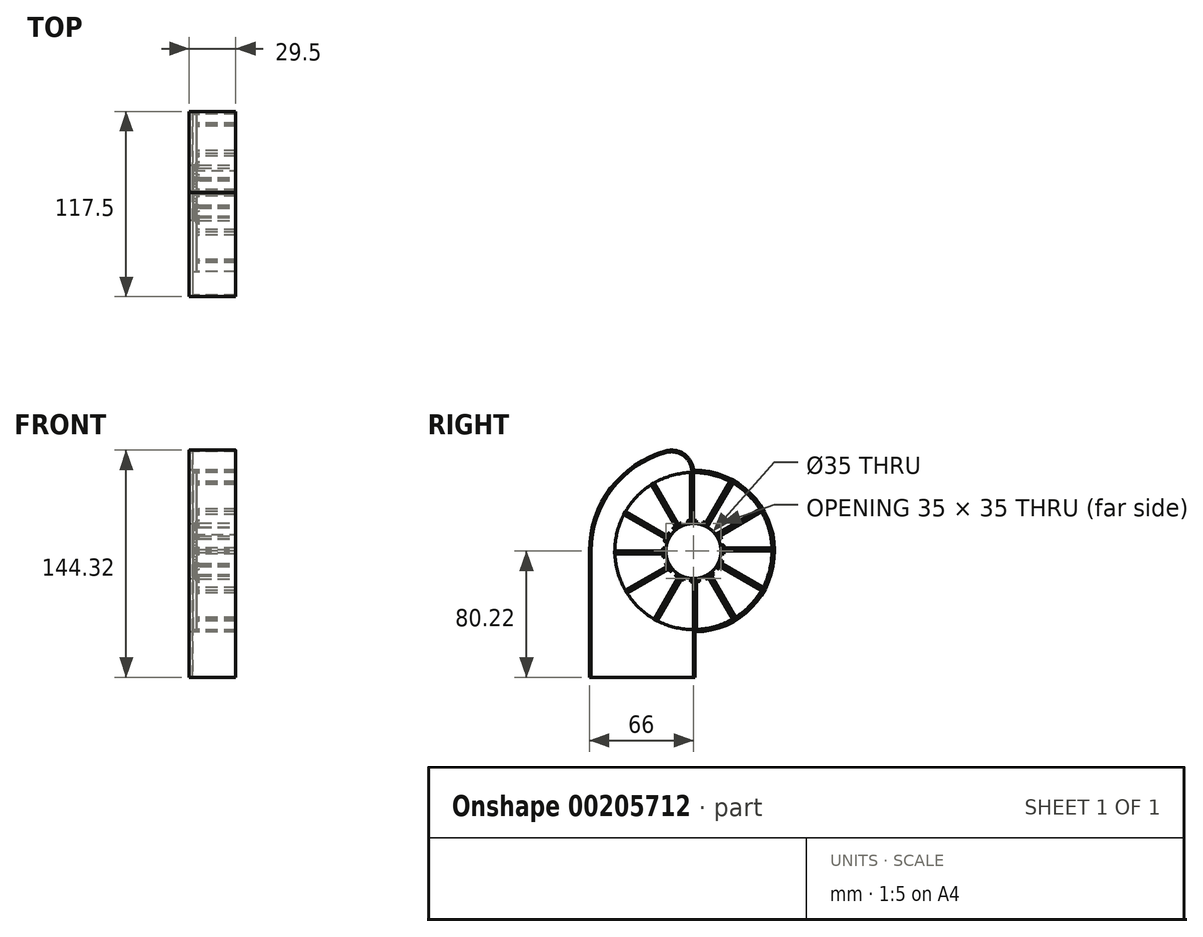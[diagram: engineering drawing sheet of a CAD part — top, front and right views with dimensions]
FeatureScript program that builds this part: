
annotation { "Feature Type Name" : "Feature", "Feature Type Description" : "" }
export const myFeature = defineFeature(function(context is Context, id is Id, definition is map)
    precondition{}
    {
        {
            var Q0;
            Q0=qCreatedBy(makeId("Front.planeOp"),FACE);
            var sketch = newSketch(context, id + "F0", { "sketchPlane" : qUnion([Q0])});
            skLineSegment(sketch, "E0", {"start": v(0, 0) * mm, "end": v(-1, 0) * mm});
            skLineSegment(sketch, "E1", {"start": v(-1, 0) * mm, "end": v(-1, 50) * mm});
            skLineSegment(sketch, "E2", {"start": v(-1, 50) * mm, "end": v(1, 50) * mm});
            skLineSegment(sketch, "E3", {"start": v(1, 50) * mm, "end": v(1, 0) * mm});
            skLineSegment(sketch, "E4", {"start": v(1, 0) * mm, "end": v(0, 0) * mm});
            skSolve(sketch);
        }
        {
            var Q0;
            Q0 = qSketchRegion(id + "F0", true);
            extrude(context, id + "F1", {"entities" : qUnion([Q0]), "depth" : 25 * mm, "offsetDistance" : 25 * mm});
        }
        {
            var Q0;
            Q0=makeQuery(id+"F1.opExtrude","SWEPT_BODY",BODY,{"disambiguationData":[OSD([sQuery(id+"F0.wireOp",EDGE,"E0"),sQuery(id+"F0.wireOp",EDGE,"E1"),sQuery(id+"F0.wireOp",EDGE,"E2"),sQuery(id+"F0.wireOp",EDGE,"E3"),sQuery(id+"F0.wireOp",EDGE,"E4")])]});
            var Q1;
            Q1=sQuery(id+"F0.wireOp",EDGE,"E1");
            var Q2;
            Q2=sQuery(id+"F0.wireOp",EDGE,"E1");
            transform(context, id + "F2", {"entities" : qUnion([Q0]), "transformType" : TransformType.ROTATION, "transformAxis" : qUnion([Q2]), "angle" : 90 * degree, "makeCopy" : false});
        }
        {
            var Q0;
            Q0=makeQuery(id+"F1.opExtrude","SWEPT_BODY",BODY,{"disambiguationData":[OSD([sQuery(id+"F0.wireOp",EDGE,"E0"),sQuery(id+"F0.wireOp",EDGE,"E1"),sQuery(id+"F0.wireOp",EDGE,"E2"),sQuery(id+"F0.wireOp",EDGE,"E3"),sQuery(id+"F0.wireOp",EDGE,"E4")])]});
            var Q1;
            Q1=makeQuery(id+"F1.opExtrude","SWEPT_EDGE",EDGE,{"disambiguationData":[OSD([sQuery(id+"F0.wireOp",EDGE,"E3"),sQuery(id+"F0.wireOp",EDGE,"E4")])]});
            circularPattern(context, id + "F3", {"entities" : qUnion([Q0]), "axis" : qUnion([Q1]), "angle" : 360 * degree, "instanceCount" : 12, "oppositeDirection" : true, "equalSpace" : true});
        }
        {
            var Q0;
            Q0=makeQuery(id+"F3.opPattern","COPY",FACE,{"derivedFrom":makeQuery(id+"F1.opExtrude","CAP_FACE",FACE,{"disambiguationData":[OSD([sQuery(id+"F0.wireOp",EDGE,"E0"),sQuery(id+"F0.wireOp",EDGE,"E1"),sQuery(id+"F0.wireOp",EDGE,"E2"),sQuery(id+"F0.wireOp",EDGE,"E3"),sQuery(id+"F0.wireOp",EDGE,"E4")])],"isStart":true}),"instanceName":"10"});
            var sketch = newSketch(context, id + "F4", { "sketchPlane" : qUnion([Q0])});
            skCircle(sketch, "E5", {"center": v(-2, 0) * mm, "radius": 49.91 * mm});
            skSolve(sketch);
        }
        {
            var Q0;
            Q0 = qSketchRegion(id + "F4", true);
            extrude(context, id + "F5", {"entities" : qUnion([Q0]), "operationType" : NewBodyOperationType.ADD, "depth" : 2 * mm, "offsetDistance" : 25 * mm});
        }
        {
            var Q0;
            Q0=makeQuery(id+"F3.opPattern","COPY",FACE,{"derivedFrom":makeQuery(id+"F1.opExtrude","CAP_FACE",FACE,{"disambiguationData":[OSD([sQuery(id+"F0.wireOp",EDGE,"E0"),sQuery(id+"F0.wireOp",EDGE,"E1"),sQuery(id+"F0.wireOp",EDGE,"E2"),sQuery(id+"F0.wireOp",EDGE,"E3"),sQuery(id+"F0.wireOp",EDGE,"E4")])],"isStart":false}),"instanceName":"9"});
            var sketch = newSketch(context, id + "F6", { "sketchPlane" : qUnion([Q0])});
            skCircle(sketch, "E6", {"center": v(2, 0) * mm, "radius": 17.5 * mm});
            skSolve(sketch);
        }
        {
            var Q0;
            Q0 = qSketchRegion(id + "F6", true);
            extrude(context, id + "F7", {"entities" : qUnion([Q0]), "operationType" : NewBodyOperationType.REMOVE, "oppositeDirection" : true, "depth" : 30 * mm, "offsetDistance" : 25 * mm});
        }
        {
            var Q0;
            {var subQ0=sQuery(id+"F0.wireOp",EDGE,"E1");Q0=makeQuery(id+"F5.boolean.opBoolean","SPLIT",EDGE,{"disambiguationData":[topologyDisambiguationEdgeConnected([makeQuery(id+"F5.opExtrude","CAP_FACE",FACE,{"disambiguationData":[OSD([sQuery(id+"F4.wireOp",EDGE,"E5")])],"isStart":true})])],"derivedFrom":makeQuery(id+"F3.opPattern","COPY",EDGE,{"derivedFrom":makeQuery(id+"F1.opExtrude","CAP_EDGE",EDGE,{"disambiguationData":[OSD([subQ0])],"isStart":true}),"instanceName":"5"})});}
            var Q1;
            {var subQ0=sQuery(id+"F0.wireOp",EDGE,"E3");Q1=makeQuery(id+"F5.boolean.opBoolean","SPLIT",EDGE,{"disambiguationData":[topologyDisambiguationEdgeConnected([makeQuery(id+"F5.opExtrude","CAP_FACE",FACE,{"disambiguationData":[OSD([sQuery(id+"F4.wireOp",EDGE,"E5")])],"isStart":true})])],"derivedFrom":makeQuery(id+"F3.opPattern","COPY",EDGE,{"derivedFrom":makeQuery(id+"F1.opExtrude","CAP_EDGE",EDGE,{"disambiguationData":[OSD([subQ0])],"isStart":true}),"instanceName":"6"})});}
            var Q2;
            {var subQ0=sQuery(id+"F0.wireOp",EDGE,"E1");Q2=makeQuery(id+"F5.boolean.opBoolean","SPLIT",EDGE,{"disambiguationData":[topologyDisambiguationEdgeConnected([makeQuery(id+"F5.opExtrude","CAP_FACE",FACE,{"disambiguationData":[OSD([sQuery(id+"F4.wireOp",EDGE,"E5")])],"isStart":true})])],"derivedFrom":makeQuery(id+"F3.opPattern","COPY",EDGE,{"derivedFrom":makeQuery(id+"F1.opExtrude","CAP_EDGE",EDGE,{"disambiguationData":[OSD([subQ0])],"isStart":true}),"instanceName":"10"})});}
            var Q3;
            {var subQ0=sQuery(id+"F0.wireOp",EDGE,"E3");Q3=makeQuery(id+"F5.boolean.opBoolean","SPLIT",EDGE,{"disambiguationData":[topologyDisambiguationEdgeConnected([makeQuery(id+"F5.opExtrude","CAP_FACE",FACE,{"disambiguationData":[OSD([sQuery(id+"F4.wireOp",EDGE,"E5")])],"isStart":true})])],"derivedFrom":makeQuery(id+"F3.opPattern","COPY",EDGE,{"derivedFrom":makeQuery(id+"F1.opExtrude","CAP_EDGE",EDGE,{"disambiguationData":[OSD([subQ0])],"isStart":true}),"instanceName":"11"})});}
            var Q4;
            {var subQ0=sQuery(id+"F0.wireOp",EDGE,"E3");Q4=makeQuery(id+"F5.boolean.opBoolean","SPLIT",EDGE,{"disambiguationData":[topologyDisambiguationEdgeConnected([makeQuery(id+"F5.opExtrude","CAP_FACE",FACE,{"disambiguationData":[OSD([sQuery(id+"F4.wireOp",EDGE,"E5")])],"isStart":true})])],"derivedFrom":makeQuery(id+"F1.opExtrude","CAP_EDGE",EDGE,{"disambiguationData":[OSD([subQ0])],"isStart":true})});}
            var Q5;
            {var subQ0=sQuery(id+"F0.wireOp",EDGE,"E1");Q5=makeQuery(id+"F5.boolean.opBoolean","SPLIT",EDGE,{"disambiguationData":[topologyDisambiguationEdgeConnected([makeQuery(id+"F5.opExtrude","CAP_FACE",FACE,{"disambiguationData":[OSD([sQuery(id+"F4.wireOp",EDGE,"E5")])],"isStart":true})])],"derivedFrom":makeQuery(id+"F3.opPattern","COPY",EDGE,{"derivedFrom":makeQuery(id+"F1.opExtrude","CAP_EDGE",EDGE,{"disambiguationData":[OSD([subQ0])],"isStart":true}),"instanceName":"11"})});}
            var Q6;
            {var subQ0=sQuery(id+"F0.wireOp",EDGE,"E1");Q6=makeQuery(id+"F5.boolean.opBoolean","SPLIT",EDGE,{"disambiguationData":[topologyDisambiguationEdgeConnected([makeQuery(id+"F5.opExtrude","CAP_FACE",FACE,{"disambiguationData":[OSD([sQuery(id+"F4.wireOp",EDGE,"E5")])],"isStart":true})])],"derivedFrom":makeQuery(id+"F1.opExtrude","CAP_EDGE",EDGE,{"disambiguationData":[OSD([subQ0])],"isStart":true})});}
            var Q7;
            {var subQ0=sQuery(id+"F0.wireOp",EDGE,"E3");Q7=makeQuery(id+"F5.boolean.opBoolean","SPLIT",EDGE,{"disambiguationData":[topologyDisambiguationEdgeConnected([makeQuery(id+"F5.opExtrude","CAP_FACE",FACE,{"disambiguationData":[OSD([sQuery(id+"F4.wireOp",EDGE,"E5")])],"isStart":true})])],"derivedFrom":makeQuery(id+"F3.opPattern","COPY",EDGE,{"derivedFrom":makeQuery(id+"F1.opExtrude","CAP_EDGE",EDGE,{"disambiguationData":[OSD([subQ0])],"isStart":true}),"instanceName":"1"})});}
            var Q8;
            {var subQ0=sQuery(id+"F0.wireOp",EDGE,"E1");Q8=makeQuery(id+"F5.boolean.opBoolean","SPLIT",EDGE,{"disambiguationData":[topologyDisambiguationEdgeConnected([makeQuery(id+"F5.opExtrude","CAP_FACE",FACE,{"disambiguationData":[OSD([sQuery(id+"F4.wireOp",EDGE,"E5")])],"isStart":true})])],"derivedFrom":makeQuery(id+"F3.opPattern","COPY",EDGE,{"derivedFrom":makeQuery(id+"F1.opExtrude","CAP_EDGE",EDGE,{"disambiguationData":[OSD([subQ0])],"isStart":true}),"instanceName":"1"})});}
            var Q9;
            {var subQ0=sQuery(id+"F0.wireOp",EDGE,"E1");Q9=makeQuery(id+"F5.boolean.opBoolean","SPLIT",EDGE,{"disambiguationData":[topologyDisambiguationEdgeConnected([makeQuery(id+"F5.opExtrude","CAP_FACE",FACE,{"disambiguationData":[OSD([sQuery(id+"F4.wireOp",EDGE,"E5")])],"isStart":true})])],"derivedFrom":makeQuery(id+"F3.opPattern","COPY",EDGE,{"derivedFrom":makeQuery(id+"F1.opExtrude","CAP_EDGE",EDGE,{"disambiguationData":[OSD([subQ0])],"isStart":true}),"instanceName":"2"})});}
            var Q10;
            {var subQ0=sQuery(id+"F0.wireOp",EDGE,"E1");Q10=makeQuery(id+"F5.boolean.opBoolean","SPLIT",EDGE,{"disambiguationData":[topologyDisambiguationEdgeConnected([makeQuery(id+"F5.opExtrude","CAP_FACE",FACE,{"disambiguationData":[OSD([sQuery(id+"F4.wireOp",EDGE,"E5")])],"isStart":true})])],"derivedFrom":makeQuery(id+"F3.opPattern","COPY",EDGE,{"derivedFrom":makeQuery(id+"F1.opExtrude","CAP_EDGE",EDGE,{"disambiguationData":[OSD([subQ0])],"isStart":true}),"instanceName":"3"})});}
            var Q11;
            {var subQ0=sQuery(id+"F0.wireOp",EDGE,"E1");Q11=makeQuery(id+"F5.boolean.opBoolean","SPLIT",EDGE,{"disambiguationData":[topologyDisambiguationEdgeConnected([makeQuery(id+"F5.opExtrude","CAP_FACE",FACE,{"disambiguationData":[OSD([sQuery(id+"F4.wireOp",EDGE,"E5")])],"isStart":true})])],"derivedFrom":makeQuery(id+"F3.opPattern","COPY",EDGE,{"derivedFrom":makeQuery(id+"F1.opExtrude","CAP_EDGE",EDGE,{"disambiguationData":[OSD([subQ0])],"isStart":true}),"instanceName":"4"})});}
            var Q12;
            {var subQ0=sQuery(id+"F0.wireOp",EDGE,"E1");Q12=makeQuery(id+"F5.boolean.opBoolean","SPLIT",EDGE,{"disambiguationData":[topologyDisambiguationEdgeConnected([makeQuery(id+"F5.opExtrude","CAP_FACE",FACE,{"disambiguationData":[OSD([sQuery(id+"F4.wireOp",EDGE,"E5")])],"isStart":true})])],"derivedFrom":makeQuery(id+"F3.opPattern","COPY",EDGE,{"derivedFrom":makeQuery(id+"F1.opExtrude","CAP_EDGE",EDGE,{"disambiguationData":[OSD([subQ0])],"isStart":true}),"instanceName":"6"})});}
            var Q13;
            {var subQ0=sQuery(id+"F0.wireOp",EDGE,"E3");Q13=makeQuery(id+"F5.boolean.opBoolean","SPLIT",EDGE,{"disambiguationData":[topologyDisambiguationEdgeConnected([makeQuery(id+"F5.opExtrude","CAP_FACE",FACE,{"disambiguationData":[OSD([sQuery(id+"F4.wireOp",EDGE,"E5")])],"isStart":true})])],"derivedFrom":makeQuery(id+"F3.opPattern","COPY",EDGE,{"derivedFrom":makeQuery(id+"F1.opExtrude","CAP_EDGE",EDGE,{"disambiguationData":[OSD([subQ0])],"isStart":true}),"instanceName":"7"})});}
            var Q14;
            Q14=makeQuery(id+"F5.boolean.opBoolean","MERGE",EDGE,{"derivedFrom":[makeQuery(id+"F3.opPattern","COPY",EDGE,{"derivedFrom":makeQuery(id+"F1.opExtrude","CAP_EDGE",EDGE,{"disambiguationData":[OSD([sQuery(id+"F0.wireOp",EDGE,"E3")])],"isStart":true}),"instanceName":"8"}),makeQuery(id+"F3.opPattern","COPY",EDGE,{"derivedFrom":makeQuery(id+"F1.opExtrude","CAP_EDGE",EDGE,{"disambiguationData":[OSD([sQuery(id+"F0.wireOp",EDGE,"E0"),sQuery(id+"F0.wireOp",EDGE,"E4")])],"isStart":true}),"instanceName":"11"})]});
            var Q15;
            {var subQ0=sQuery(id+"F0.wireOp",EDGE,"E3");Q15=makeQuery(id+"F5.boolean.opBoolean","SPLIT",EDGE,{"disambiguationData":[topologyDisambiguationEdgeConnected([makeQuery(id+"F5.opExtrude","CAP_FACE",FACE,{"disambiguationData":[OSD([sQuery(id+"F4.wireOp",EDGE,"E5")])],"isStart":true})])],"derivedFrom":makeQuery(id+"F3.opPattern","COPY",EDGE,{"derivedFrom":makeQuery(id+"F1.opExtrude","CAP_EDGE",EDGE,{"disambiguationData":[OSD([subQ0])],"isStart":true}),"instanceName":"9"})});}
            var Q16;
            {var subQ0=sQuery(id+"F0.wireOp",EDGE,"E3");Q16=makeQuery(id+"F5.boolean.opBoolean","SPLIT",EDGE,{"disambiguationData":[topologyDisambiguationEdgeConnected([makeQuery(id+"F5.opExtrude","CAP_FACE",FACE,{"disambiguationData":[OSD([sQuery(id+"F4.wireOp",EDGE,"E5")])],"isStart":true})])],"derivedFrom":makeQuery(id+"F3.opPattern","COPY",EDGE,{"derivedFrom":makeQuery(id+"F1.opExtrude","CAP_EDGE",EDGE,{"disambiguationData":[OSD([subQ0])],"isStart":true}),"instanceName":"10"})});}
            var Q17;
            {var subQ0=sQuery(id+"F0.wireOp",EDGE,"E3");Q17=makeQuery(id+"F5.boolean.opBoolean","SPLIT",EDGE,{"disambiguationData":[topologyDisambiguationEdgeConnected([makeQuery(id+"F5.opExtrude","CAP_FACE",FACE,{"disambiguationData":[OSD([sQuery(id+"F4.wireOp",EDGE,"E5")])],"isStart":true})])],"derivedFrom":makeQuery(id+"F3.opPattern","COPY",EDGE,{"derivedFrom":makeQuery(id+"F1.opExtrude","CAP_EDGE",EDGE,{"disambiguationData":[OSD([subQ0])],"isStart":true}),"instanceName":"2"})});}
            var Q18;
            {var subQ0=sQuery(id+"F0.wireOp",EDGE,"E3");Q18=makeQuery(id+"F5.boolean.opBoolean","SPLIT",EDGE,{"disambiguationData":[topologyDisambiguationEdgeConnected([makeQuery(id+"F5.opExtrude","CAP_FACE",FACE,{"disambiguationData":[OSD([sQuery(id+"F4.wireOp",EDGE,"E5")])],"isStart":true})])],"derivedFrom":makeQuery(id+"F3.opPattern","COPY",EDGE,{"derivedFrom":makeQuery(id+"F1.opExtrude","CAP_EDGE",EDGE,{"disambiguationData":[OSD([subQ0])],"isStart":true}),"instanceName":"3"})});}
            var Q19;
            {var subQ0=sQuery(id+"F0.wireOp",EDGE,"E1");Q19=makeQuery(id+"F5.boolean.opBoolean","SPLIT",EDGE,{"disambiguationData":[topologyDisambiguationEdgeConnected([makeQuery(id+"F5.opExtrude","CAP_FACE",FACE,{"disambiguationData":[OSD([sQuery(id+"F4.wireOp",EDGE,"E5")])],"isStart":true})])],"derivedFrom":makeQuery(id+"F3.opPattern","COPY",EDGE,{"derivedFrom":makeQuery(id+"F1.opExtrude","CAP_EDGE",EDGE,{"disambiguationData":[OSD([subQ0])],"isStart":true}),"instanceName":"8"})});}
            var Q20;
            {var subQ0=sQuery(id+"F0.wireOp",EDGE,"E1");Q20=makeQuery(id+"F5.boolean.opBoolean","SPLIT",EDGE,{"disambiguationData":[topologyDisambiguationEdgeConnected([makeQuery(id+"F5.opExtrude","CAP_FACE",FACE,{"disambiguationData":[OSD([sQuery(id+"F4.wireOp",EDGE,"E5")])],"isStart":true})])],"derivedFrom":makeQuery(id+"F3.opPattern","COPY",EDGE,{"derivedFrom":makeQuery(id+"F1.opExtrude","CAP_EDGE",EDGE,{"disambiguationData":[OSD([subQ0])],"isStart":true}),"instanceName":"9"})});}
            var Q21;
            {var subQ0=sQuery(id+"F0.wireOp",EDGE,"E1");Q21=makeQuery(id+"F5.boolean.opBoolean","SPLIT",EDGE,{"disambiguationData":[topologyDisambiguationEdgeConnected([makeQuery(id+"F5.opExtrude","CAP_FACE",FACE,{"disambiguationData":[OSD([sQuery(id+"F4.wireOp",EDGE,"E5")])],"isStart":true})])],"derivedFrom":makeQuery(id+"F3.opPattern","COPY",EDGE,{"derivedFrom":makeQuery(id+"F1.opExtrude","CAP_EDGE",EDGE,{"disambiguationData":[OSD([subQ0])],"isStart":true}),"instanceName":"7"})});}
            var Q22;
            {var subQ0=sQuery(id+"F0.wireOp",EDGE,"E3");Q22=makeQuery(id+"F5.boolean.opBoolean","SPLIT",EDGE,{"disambiguationData":[topologyDisambiguationEdgeConnected([makeQuery(id+"F5.opExtrude","CAP_FACE",FACE,{"disambiguationData":[OSD([sQuery(id+"F4.wireOp",EDGE,"E5")])],"isStart":true})])],"derivedFrom":makeQuery(id+"F3.opPattern","COPY",EDGE,{"derivedFrom":makeQuery(id+"F1.opExtrude","CAP_EDGE",EDGE,{"disambiguationData":[OSD([subQ0])],"isStart":true}),"instanceName":"5"})});}
            var Q23;
            {var subQ0=sQuery(id+"F0.wireOp",EDGE,"E3");Q23=makeQuery(id+"F5.boolean.opBoolean","SPLIT",EDGE,{"disambiguationData":[topologyDisambiguationEdgeConnected([makeQuery(id+"F5.opExtrude","CAP_FACE",FACE,{"disambiguationData":[OSD([sQuery(id+"F4.wireOp",EDGE,"E5")])],"isStart":true})])],"derivedFrom":makeQuery(id+"F3.opPattern","COPY",EDGE,{"derivedFrom":makeQuery(id+"F1.opExtrude","CAP_EDGE",EDGE,{"disambiguationData":[OSD([subQ0])],"isStart":true}),"instanceName":"4"})});}
            fillet(context, id + "F8", {"entities" : qUnion([Q0, Q1, Q2, Q3, Q4, Q5, Q6, Q7, Q8, Q9, Q10, Q11, Q12, Q13, Q14, Q15, Q16, Q17, Q18, Q19, Q20, Q21, Q22, Q23]), "radius" : 2 * mm, "tangentPropagation" : true, "allowEdgeOverflow" : false});
        }
        {
            var Q0;
            {var subQ0=sQuery(id+"F0.wireOp",EDGE,"E1");Q0=makeQuery(id+"F8.opFillet","BLEND_EDGE",EDGE,{"blendedFrom":[makeQuery(id+"F5.boolean.opBoolean","SPLIT",EDGE,{"disambiguationData":[topologyDisambiguationEdgeConnected([makeQuery(id+"F5.opExtrude","CAP_FACE",FACE,{"disambiguationData":[OSD([sQuery(id+"F4.wireOp",EDGE,"E5")])],"isStart":true})])],"derivedFrom":makeQuery(id+"F3.opPattern","COPY",EDGE,{"derivedFrom":makeQuery(id+"F1.opExtrude","CAP_EDGE",EDGE,{"disambiguationData":[OSD([subQ0])],"isStart":true}),"instanceName":"4"})}),makeQuery(id+"F7.boolean.opBoolean","COPY",FACE,{"derivedFrom":makeQuery(id+"F7.opExtrude","SWEPT_FACE",FACE,{"disambiguationData":[OSD([sQuery(id+"F6.wireOp",EDGE,"E6")])]})})],"blendedInto":[makeQuery(id+"F7.boolean.opBoolean","COPY",FACE,{"derivedFrom":makeQuery(id+"F7.opExtrude","SWEPT_FACE",FACE,{"disambiguationData":[OSD([sQuery(id+"F6.wireOp",EDGE,"E6")])]})})]});}
            var Q1;
            {var subQ1=sQuery(id+"F0.wireOp",EDGE,"E1");var subQ3=sQuery(id+"F4.wireOp",EDGE,"E5");Q1=makeQuery(id+"F7.boolean.opBoolean","INTERSECT",EDGE,{"derivedFrom":[makeQuery(id+"F5.boolean.opBoolean","SPLIT",FACE,{"disambiguationData":[TD([makeQuery(id+"F3.opPattern","COPY",FACE,{"derivedFrom":makeQuery(id+"F1.opExtrude","SWEPT_FACE",FACE,{"disambiguationData":[OSD([subQ1])]}),"instanceName":"3"})])],"derivedFrom":makeQuery(id+"F5.opExtrude","CAP_FACE",FACE,{"disambiguationData":[OSD([subQ3])],"isStart":true})}),makeQuery(id+"F7.opExtrude","SWEPT_FACE",FACE,{"disambiguationData":[OSD([sQuery(id+"F6.wireOp",EDGE,"E6")])]})]});}
            var Q2;
            {var subQ1=sQuery(id+"F0.wireOp",EDGE,"E1");var subQ3=sQuery(id+"F4.wireOp",EDGE,"E5");Q2=makeQuery(id+"F7.boolean.opBoolean","INTERSECT",EDGE,{"derivedFrom":[makeQuery(id+"F5.boolean.opBoolean","SPLIT",FACE,{"disambiguationData":[TD([makeQuery(id+"F3.opPattern","COPY",FACE,{"derivedFrom":makeQuery(id+"F1.opExtrude","SWEPT_FACE",FACE,{"disambiguationData":[OSD([subQ1])]}),"instanceName":"2"})])],"derivedFrom":makeQuery(id+"F5.opExtrude","CAP_FACE",FACE,{"disambiguationData":[OSD([subQ3])],"isStart":true})}),makeQuery(id+"F7.opExtrude","SWEPT_FACE",FACE,{"disambiguationData":[OSD([sQuery(id+"F6.wireOp",EDGE,"E6")])]})]});}
            var Q3;
            {var subQ0=sQuery(id+"F0.wireOp",EDGE,"E1");Q3=makeQuery(id+"F8.opFillet","BLEND_EDGE",EDGE,{"blendedFrom":[makeQuery(id+"F5.boolean.opBoolean","SPLIT",EDGE,{"disambiguationData":[topologyDisambiguationEdgeConnected([makeQuery(id+"F5.opExtrude","CAP_FACE",FACE,{"disambiguationData":[OSD([sQuery(id+"F4.wireOp",EDGE,"E5")])],"isStart":true})])],"derivedFrom":makeQuery(id+"F3.opPattern","COPY",EDGE,{"derivedFrom":makeQuery(id+"F1.opExtrude","CAP_EDGE",EDGE,{"disambiguationData":[OSD([subQ0])],"isStart":true}),"instanceName":"5"})}),makeQuery(id+"F7.boolean.opBoolean","COPY",FACE,{"derivedFrom":makeQuery(id+"F7.opExtrude","SWEPT_FACE",FACE,{"disambiguationData":[OSD([sQuery(id+"F6.wireOp",EDGE,"E6")])]})})],"blendedInto":[makeQuery(id+"F7.boolean.opBoolean","COPY",FACE,{"derivedFrom":makeQuery(id+"F7.opExtrude","SWEPT_FACE",FACE,{"disambiguationData":[OSD([sQuery(id+"F6.wireOp",EDGE,"E6")])]})})]});}
            var Q4;
            {var subQ0=sQuery(id+"F0.wireOp",EDGE,"E1");Q4=makeQuery(id+"F8.opFillet","BLEND_EDGE",EDGE,{"blendedFrom":[makeQuery(id+"F5.boolean.opBoolean","SPLIT",EDGE,{"disambiguationData":[topologyDisambiguationEdgeConnected([makeQuery(id+"F5.opExtrude","CAP_FACE",FACE,{"disambiguationData":[OSD([sQuery(id+"F4.wireOp",EDGE,"E5")])],"isStart":true})])],"derivedFrom":makeQuery(id+"F3.opPattern","COPY",EDGE,{"derivedFrom":makeQuery(id+"F1.opExtrude","CAP_EDGE",EDGE,{"disambiguationData":[OSD([subQ0])],"isStart":true}),"instanceName":"6"})}),makeQuery(id+"F7.boolean.opBoolean","COPY",FACE,{"derivedFrom":makeQuery(id+"F7.opExtrude","SWEPT_FACE",FACE,{"disambiguationData":[OSD([sQuery(id+"F6.wireOp",EDGE,"E6")])]})})],"blendedInto":[makeQuery(id+"F7.boolean.opBoolean","COPY",FACE,{"derivedFrom":makeQuery(id+"F7.opExtrude","SWEPT_FACE",FACE,{"disambiguationData":[OSD([sQuery(id+"F6.wireOp",EDGE,"E6")])]})})]});}
            var Q5;
            {var subQ0=sQuery(id+"F0.wireOp",EDGE,"E1");Q5=makeQuery(id+"F8.opFillet","BLEND_EDGE",EDGE,{"blendedFrom":[makeQuery(id+"F5.boolean.opBoolean","SPLIT",EDGE,{"disambiguationData":[topologyDisambiguationEdgeConnected([makeQuery(id+"F5.opExtrude","CAP_FACE",FACE,{"disambiguationData":[OSD([sQuery(id+"F4.wireOp",EDGE,"E5")])],"isStart":true})])],"derivedFrom":makeQuery(id+"F3.opPattern","COPY",EDGE,{"derivedFrom":makeQuery(id+"F1.opExtrude","CAP_EDGE",EDGE,{"disambiguationData":[OSD([subQ0])],"isStart":true}),"instanceName":"7"})}),makeQuery(id+"F7.boolean.opBoolean","COPY",FACE,{"derivedFrom":makeQuery(id+"F7.opExtrude","SWEPT_FACE",FACE,{"disambiguationData":[OSD([sQuery(id+"F6.wireOp",EDGE,"E6")])]})})],"blendedInto":[makeQuery(id+"F7.boolean.opBoolean","COPY",FACE,{"derivedFrom":makeQuery(id+"F7.opExtrude","SWEPT_FACE",FACE,{"disambiguationData":[OSD([sQuery(id+"F6.wireOp",EDGE,"E6")])]})})]});}
            var Q6;
            {var subQ0=sQuery(id+"F0.wireOp",EDGE,"E3");Q6=makeQuery(id+"F8.opFillet","BLEND_EDGE",EDGE,{"blendedFrom":[makeQuery(id+"F5.boolean.opBoolean","SPLIT",EDGE,{"disambiguationData":[topologyDisambiguationEdgeConnected([makeQuery(id+"F5.opExtrude","CAP_FACE",FACE,{"disambiguationData":[OSD([sQuery(id+"F4.wireOp",EDGE,"E5")])],"isStart":true})])],"derivedFrom":makeQuery(id+"F3.opPattern","COPY",EDGE,{"derivedFrom":makeQuery(id+"F1.opExtrude","CAP_EDGE",EDGE,{"disambiguationData":[OSD([subQ0])],"isStart":true}),"instanceName":"2"})}),makeQuery(id+"F7.boolean.opBoolean","COPY",FACE,{"derivedFrom":makeQuery(id+"F7.opExtrude","SWEPT_FACE",FACE,{"disambiguationData":[OSD([sQuery(id+"F6.wireOp",EDGE,"E6")])]})})],"blendedInto":[makeQuery(id+"F7.boolean.opBoolean","COPY",FACE,{"derivedFrom":makeQuery(id+"F7.opExtrude","SWEPT_FACE",FACE,{"disambiguationData":[OSD([sQuery(id+"F6.wireOp",EDGE,"E6")])]})})]});}
            var Q7;
            {var subQ0=sQuery(id+"F0.wireOp",EDGE,"E3");Q7=makeQuery(id+"F8.opFillet","BLEND_EDGE",EDGE,{"blendedFrom":[makeQuery(id+"F5.boolean.opBoolean","SPLIT",EDGE,{"disambiguationData":[topologyDisambiguationEdgeConnected([makeQuery(id+"F5.opExtrude","CAP_FACE",FACE,{"disambiguationData":[OSD([sQuery(id+"F4.wireOp",EDGE,"E5")])],"isStart":true})])],"derivedFrom":makeQuery(id+"F3.opPattern","COPY",EDGE,{"derivedFrom":makeQuery(id+"F1.opExtrude","CAP_EDGE",EDGE,{"disambiguationData":[OSD([subQ0])],"isStart":true}),"instanceName":"9"})}),makeQuery(id+"F7.boolean.opBoolean","COPY",FACE,{"derivedFrom":makeQuery(id+"F7.opExtrude","SWEPT_FACE",FACE,{"disambiguationData":[OSD([sQuery(id+"F6.wireOp",EDGE,"E6")])]})})],"blendedInto":[makeQuery(id+"F7.boolean.opBoolean","COPY",FACE,{"derivedFrom":makeQuery(id+"F7.opExtrude","SWEPT_FACE",FACE,{"disambiguationData":[OSD([sQuery(id+"F6.wireOp",EDGE,"E6")])]})})]});}
            var Q8;
            {var subQ0=sQuery(id+"F0.wireOp",EDGE,"E3");Q8=makeQuery(id+"F8.opFillet","BLEND_EDGE",EDGE,{"blendedFrom":[makeQuery(id+"F5.boolean.opBoolean","SPLIT",EDGE,{"disambiguationData":[topologyDisambiguationEdgeConnected([makeQuery(id+"F5.opExtrude","CAP_FACE",FACE,{"disambiguationData":[OSD([sQuery(id+"F4.wireOp",EDGE,"E5")])],"isStart":true})])],"derivedFrom":makeQuery(id+"F3.opPattern","COPY",EDGE,{"derivedFrom":makeQuery(id+"F1.opExtrude","CAP_EDGE",EDGE,{"disambiguationData":[OSD([subQ0])],"isStart":true}),"instanceName":"10"})}),makeQuery(id+"F7.boolean.opBoolean","COPY",FACE,{"derivedFrom":makeQuery(id+"F7.opExtrude","SWEPT_FACE",FACE,{"disambiguationData":[OSD([sQuery(id+"F6.wireOp",EDGE,"E6")])]})})],"blendedInto":[makeQuery(id+"F7.boolean.opBoolean","COPY",FACE,{"derivedFrom":makeQuery(id+"F7.opExtrude","SWEPT_FACE",FACE,{"disambiguationData":[OSD([sQuery(id+"F6.wireOp",EDGE,"E6")])]})})]});}
            var Q9;
            {var subQ1=sQuery(id+"F0.wireOp",EDGE,"E1");var subQ3=sQuery(id+"F4.wireOp",EDGE,"E5");Q9=makeQuery(id+"F7.boolean.opBoolean","INTERSECT",EDGE,{"derivedFrom":[makeQuery(id+"F5.boolean.opBoolean","SPLIT",FACE,{"disambiguationData":[TD([makeQuery(id+"F3.opPattern","COPY",FACE,{"derivedFrom":makeQuery(id+"F1.opExtrude","SWEPT_FACE",FACE,{"disambiguationData":[OSD([subQ1])]}),"instanceName":"10"})])],"derivedFrom":makeQuery(id+"F5.opExtrude","CAP_FACE",FACE,{"disambiguationData":[OSD([subQ3])],"isStart":true})}),makeQuery(id+"F7.opExtrude","SWEPT_FACE",FACE,{"disambiguationData":[OSD([sQuery(id+"F6.wireOp",EDGE,"E6")])]})]});}
            var Q10;
            {var subQ0=sQuery(id+"F0.wireOp",EDGE,"E3");var subQ3=sQuery(id+"F4.wireOp",EDGE,"E5");Q10=makeQuery(id+"F7.boolean.opBoolean","INTERSECT",EDGE,{"derivedFrom":[makeQuery(id+"F5.boolean.opBoolean","SPLIT",FACE,{"disambiguationData":[TD([makeQuery(id+"F1.opExtrude","SWEPT_FACE",FACE,{"disambiguationData":[OSD([subQ0])]})])],"derivedFrom":makeQuery(id+"F5.opExtrude","CAP_FACE",FACE,{"disambiguationData":[OSD([subQ3])],"isStart":true})}),makeQuery(id+"F7.opExtrude","SWEPT_FACE",FACE,{"disambiguationData":[OSD([sQuery(id+"F6.wireOp",EDGE,"E6")])]})]});}
            var Q11;
            {var subQ1=sQuery(id+"F0.wireOp",EDGE,"E1");var subQ3=sQuery(id+"F4.wireOp",EDGE,"E5");Q11=makeQuery(id+"F7.boolean.opBoolean","INTERSECT",EDGE,{"derivedFrom":[makeQuery(id+"F5.boolean.opBoolean","SPLIT",FACE,{"disambiguationData":[TD([makeQuery(id+"F1.opExtrude","SWEPT_FACE",FACE,{"disambiguationData":[OSD([subQ1])]})])],"derivedFrom":makeQuery(id+"F5.opExtrude","CAP_FACE",FACE,{"disambiguationData":[OSD([subQ3])],"isStart":true})}),makeQuery(id+"F7.opExtrude","SWEPT_FACE",FACE,{"disambiguationData":[OSD([sQuery(id+"F6.wireOp",EDGE,"E6")])]})]});}
            fillet(context, id + "F9", {"entities" : qUnion([Q0, Q1, Q2, Q3, Q4, Q5, Q6, Q7, Q8, Q9, Q10, Q11]), "radius" : 2 * mm, "tangentPropagation" : true, "allowEdgeOverflow" : false});
        }
        {
            var Q0;
            {var subQ1=sQuery(id+"F0.wireOp",EDGE,"E1");var subQ3=sQuery(id+"F4.wireOp",EDGE,"E5");Q0=makeQuery(id+"F5.boolean.opBoolean","SPLIT",FACE,{"disambiguationData":[TD([makeQuery(id+"F1.opExtrude","SWEPT_FACE",FACE,{"disambiguationData":[OSD([subQ1])]})])],"derivedFrom":makeQuery(id+"F5.opExtrude","CAP_FACE",FACE,{"disambiguationData":[OSD([subQ3])],"isStart":true})});}
            var sketch = newSketch(context, id + "F10", { "sketchPlane" : qUnion([Q0])});
            skArc(sketch, "E7", {"start": v(2, -50.5) * mm, "mid": v(52.5, 0) * mm, "end": v(2, 50.5) * mm});
            skArc(sketch, "E8", {"start": v(1, 65) * mm, "mid": v(-44.31, 45.6) * mm, "end": v(-63, 0) * mm});
            skLineSegment(sketch, "E9", {"start": v(2, 65) * mm, "end": v(2, 51.5) * mm});
            skLineSegment(sketch, "E10", {"start": v(2, -80.22) * mm, "end": v(2, -50.5) * mm});
            skLineSegment(sketch, "E11", {"start": v(-63, 0) * mm, "end": v(-63, -80.22) * mm});
            skLineSegment(sketch, "E12", {"start": v(-63, -80.22) * mm, "end": v(2, -80.22) * mm});
            skArc(sketch, "E13.0", {"start": v(2, 66) * mm, "mid": v(-44.67, 46.67) * mm, "end": v(-64, 0) * mm});
            skLineSegment(sketch, "E14.0", {"start": v(-64, 0) * mm, "end": v(-64, -80.22) * mm});
            skLineSegment(sketch, "E15.0", {"start": v(3, -80.22) * mm, "end": v(3, -51.5) * mm});
            skArc(sketch, "E16.0", {"start": v(3, -51.5) * mm, "mid": v(53.5, 0.5) * mm, "end": v(2, 51.5) * mm});
            skLineSegment(sketch, "E17.0", {"start": v(1, 65) * mm, "end": v(1, 50.5) * mm});
            skLineSegment(sketch, "E18", {"start": v(2, 50.5) * mm, "end": v(1, 50.5) * mm});
            skLineSegment(sketch, "E19", {"start": v(2, 65) * mm, "end": v(2, 66) * mm});
            skLineSegment(sketch, "E20", {"start": v(-64, -80.22) * mm, "end": v(-63, -80.22) * mm});
            skLineSegment(sketch, "E21", {"start": v(2, -80.22) * mm, "end": v(3, -80.22) * mm});
            skSolve(sketch);
        }
        {
            var Q0;
            Q0=makeQuery(id+"F10.imprint","IMPRINT",FACE,{"disambiguationData":[TD([[makeQuery(id+"F10.imprint","IMPRINT",EDGE,{"derivedFrom":sQuery(id+"F10.wireOp",EDGE,"E7")}),-1.0]])]});
            extrude(context, id + "F11", {"entities" : qUnion([Q0]), "depth" : 25 * mm, "offsetDistance" : 25 * mm});
        }
        {
            var Q0;
            Q0=makeQuery(id+"F11.opExtrude","SWEPT_EDGE",EDGE,{"disambiguationData":[OSD([sQuery(id+"F10.wireOp",EDGE,"E8"),sQuery(id+"F10.wireOp",EDGE,"E17.0")])]});
            fillet(context, id + "F12", {"entities" : qUnion([Q0]), "radius" : 13 * mm, "tangentPropagation" : true, "allowEdgeOverflow" : false});
        }
        {
            var Q0;
            Q0=makeQuery(id+"F11.opExtrude","SWEPT_EDGE",EDGE,{"disambiguationData":[OSD([sQuery(id+"F10.wireOp",EDGE,"E13.0"),sQuery(id+"F10.wireOp",EDGE,"E19")])]});
            fillet(context, id + "F13", {"entities" : qUnion([Q0]), "radius" : 14 * mm, "tangentPropagation" : true, "allowEdgeOverflow" : false});
        }
        {
            var Q0;
            Q0=makeQuery(id+"F11.opExtrude","CAP_FACE",FACE,{"disambiguationData":[OSD([sQuery(id+"F10.wireOp",EDGE,"E7"),sQuery(id+"F10.wireOp",EDGE,"E8"),sQuery(id+"F10.wireOp",EDGE,"E9"),sQuery(id+"F10.wireOp",EDGE,"E10"),sQuery(id+"F10.wireOp",EDGE,"E11"),sQuery(id+"F10.wireOp",EDGE,"E13.0"),sQuery(id+"F10.wireOp",EDGE,"E14.0"),sQuery(id+"F10.wireOp",EDGE,"E15.0"),sQuery(id+"F10.wireOp",EDGE,"E16.0"),sQuery(id+"F10.wireOp",EDGE,"E17.0"),sQuery(id+"F10.wireOp",EDGE,"E18"),sQuery(id+"F10.wireOp",EDGE,"E19"),sQuery(id+"F10.wireOp",EDGE,"E20"),sQuery(id+"F10.wireOp",EDGE,"E21")])],"isStart":true});
            extrude(context, id + "F14", {"entities" : qUnion([Q0]), "operationType" : NewBodyOperationType.ADD, "depth" : 4.5 * mm, "offsetDistance" : 25 * mm});
        }
        {
            var Q0;
            Q0=makeQuery(id+"F14.opExtrude","CAP_FACE",FACE,{"disambiguationData":[OSD([sQuery(id+"F10.wireOp",EDGE,"E7"),sQuery(id+"F10.wireOp",EDGE,"E8"),sQuery(id+"F10.wireOp",EDGE,"E9"),sQuery(id+"F10.wireOp",EDGE,"E10"),sQuery(id+"F10.wireOp",EDGE,"E11"),sQuery(id+"F10.wireOp",EDGE,"E13.0"),sQuery(id+"F10.wireOp",EDGE,"E14.0"),sQuery(id+"F10.wireOp",EDGE,"E15.0"),sQuery(id+"F10.wireOp",EDGE,"E16.0"),sQuery(id+"F10.wireOp",EDGE,"E17.0"),sQuery(id+"F10.wireOp",EDGE,"E18"),sQuery(id+"F10.wireOp",EDGE,"E19"),sQuery(id+"F10.wireOp",EDGE,"E20"),sQuery(id+"F10.wireOp",EDGE,"E21")])],"isStart":false});
            var sketch = newSketch(context, id + "F15", { "sketchPlane" : qUnion([Q0])});
            skLineSegment(sketch, "E22", {"start": v(-2, -80.22) * mm, "end": v(63, -80.22) * mm});
            skSolve(sketch);
        }
        {
            var Q0;
            Q0=makeQuery(id+"F15.imprint","IMPRINT",FACE,{"disambiguationData":[TD([[makeQuery(id+"F15.imprint","IMPRINT",EDGE,{"derivedFrom":sQuery(id+"F15.wireOp",EDGE,"E22")}),1.0]])]});
            extrude(context, id + "F16", {"entities" : qUnion([Q0]), "operationType" : NewBodyOperationType.ADD, "oppositeDirection" : true, "depth" : 2 * mm, "offsetDistance" : 25 * mm});
        }
        {
            var Q0;
            {var subQ0=sQuery(id+"F0.wireOp",EDGE,"E1");var subQ1=sQuery(id+"F0.wireOp",EDGE,"E2");var subQ2=sQuery(id+"F0.wireOp",EDGE,"E3");var subQ3=makeQuery(id+"F1.opExtrude","CAP_FACE",FACE,{"disambiguationData":[OSD([sQuery(id+"F0.wireOp",EDGE,"E0"),subQ0,subQ1,subQ2,sQuery(id+"F0.wireOp",EDGE,"E4")])],"isStart":false});Q0=makeQuery(id+"F7.boolean.opBoolean","SPLIT",FACE,{"disambiguationData":[TD([makeQuery(id+"F3.opPattern","COPY",FACE,{"derivedFrom":makeQuery(id+"F1.opExtrude","SWEPT_FACE",FACE,{"disambiguationData":[OSD([subQ0])]}),"instanceName":"9"})])],"derivedFrom":makeQuery(id+"F5.boolean.opBoolean","MERGE",FACE,{"derivedFrom":[subQ3,makeQuery(id+"F3.opPattern","COPY",FACE,{"derivedFrom":subQ3,"instanceName":"1"}),makeQuery(id+"F3.opPattern","COPY",FACE,{"derivedFrom":subQ3,"instanceName":"2"}),makeQuery(id+"F3.opPattern","COPY",FACE,{"derivedFrom":subQ3,"instanceName":"3"}),makeQuery(id+"F3.opPattern","COPY",FACE,{"derivedFrom":subQ3,"instanceName":"4"}),makeQuery(id+"F3.opPattern","COPY",FACE,{"derivedFrom":subQ3,"instanceName":"5"}),makeQuery(id+"F3.opPattern","COPY",FACE,{"derivedFrom":subQ3,"instanceName":"6"}),makeQuery(id+"F3.opPattern","COPY",FACE,{"derivedFrom":subQ3,"instanceName":"7"}),makeQuery(id+"F3.opPattern","COPY",FACE,{"derivedFrom":subQ3,"instanceName":"8"}),makeQuery(id+"F3.opPattern","COPY",FACE,{"derivedFrom":subQ3,"instanceName":"9"}),makeQuery(id+"F3.opPattern","COPY",FACE,{"derivedFrom":subQ3,"instanceName":"10"}),makeQuery(id+"F3.opPattern","COPY",FACE,{"derivedFrom":subQ3,"instanceName":"11"})]})});}
            var sketch = newSketch(context, id + "F17", { "sketchPlane" : qUnion([Q0])});
            skCircle(sketch, "E23", {"center": v(2, 0) * mm, "radius": 17.5 * mm});
            skSolve(sketch);
        }
        {
            var Q0;
            Q0 = qSketchRegion(id + "F17", true);
            extrude(context, id + "F18", {"entities" : qUnion([Q0]), "operationType" : NewBodyOperationType.REMOVE, "oppositeDirection" : true, "depth" : 50 * mm, "offsetDistance" : 25 * mm});
        }
    });
